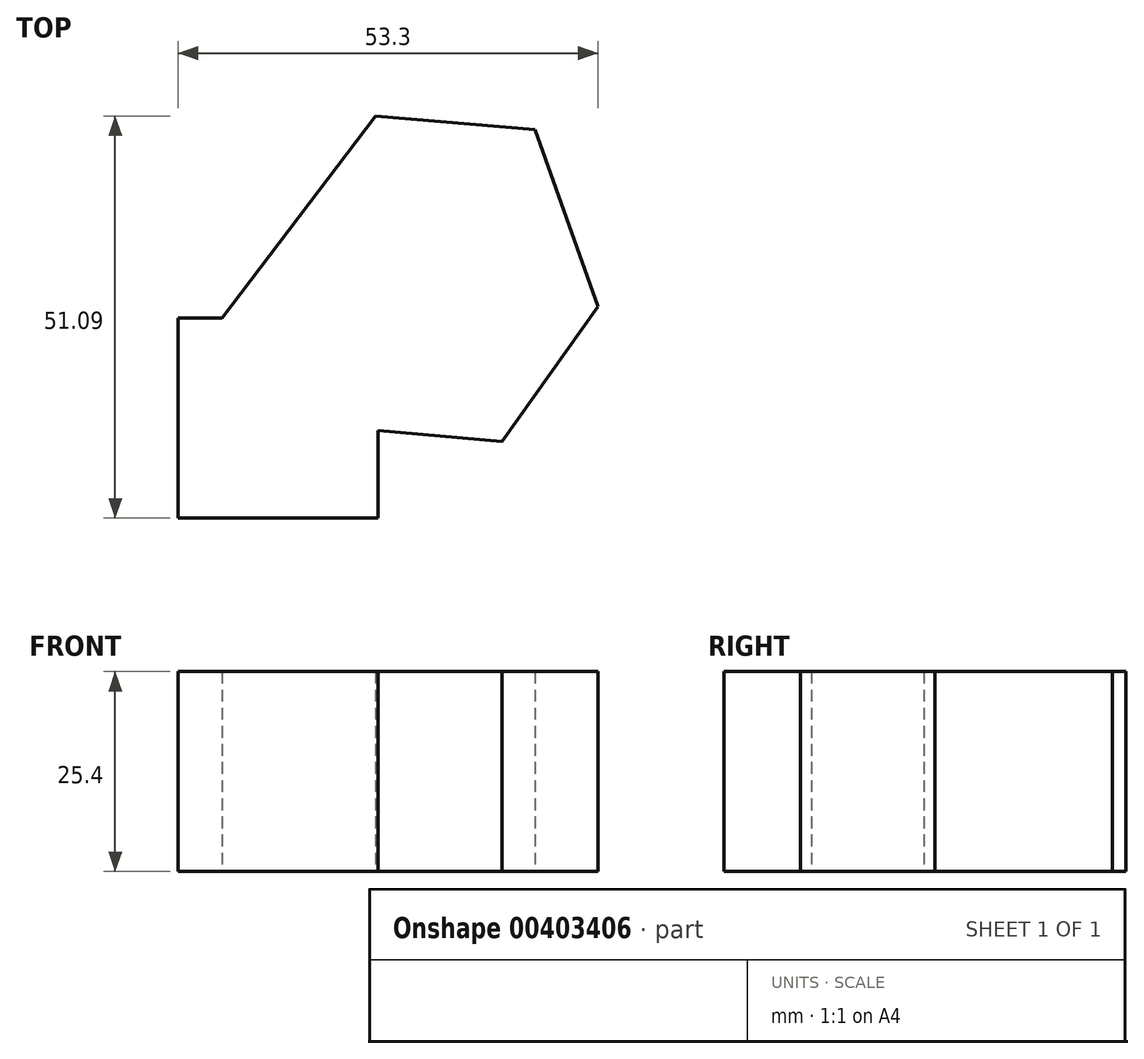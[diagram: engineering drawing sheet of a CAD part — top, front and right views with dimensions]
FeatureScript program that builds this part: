
annotation { "Feature Type Name" : "Feature", "Feature Type Description" : "" }
export const myFeature = defineFeature(function(context is Context, id is Id, definition is map)
    precondition{}
    {
        {
            var Q0;
            Q0=qCreatedBy(makeId("Top.planeOp"),FACE);
            var sketch = newSketch(context, id + "F0", { "sketchPlane" : qUnion([Q0])});
            skLineSegment(sketch, "E0.bottom", {"start": v(-30.25, -38.77) * mm, "end": v(-4.85, -38.77) * mm});
            skLineSegment(sketch, "E0.top", {"start": v(-30.25, -13.37) * mm, "end": v(-4.85, -13.37) * mm});
            skLineSegment(sketch, "E0.left", {"start": v(-30.25, -38.77) * mm, "end": v(-30.25, -13.37) * mm});
            skLineSegment(sketch, "E0.right", {"start": v(-4.85, -38.77) * mm, "end": v(-4.85, -13.37) * mm});
            skLineSegment(sketch, "E1", {"start": v(-26.63, -15.9) * mm, "end": v(-5.17, 12.32) * mm});
            skLineSegment(sketch, "E2", {"start": v(-5.17, 12.32) * mm, "end": v(15.1, 10.6) * mm});
            skLineSegment(sketch, "E3", {"start": v(15.1, 10.6) * mm, "end": v(23.05, -11.92) * mm});
            skLineSegment(sketch, "E4", {"start": v(23.05, -11.92) * mm, "end": v(10.86, -29.01) * mm});
            skLineSegment(sketch, "E5", {"start": v(10.86, -29.01) * mm, "end": v(-8.61, -27.29) * mm});
            skLineSegment(sketch, "E6", {"start": v(-8.61, -27.29) * mm, "end": v(-26.63, -15.9) * mm});
            skSolve(sketch);
        }
        {
            var Q0;
            {var subQ0=sQuery(id+"F0.wireOp",EDGE,"E6");Q0=makeQuery(id+"F0.imprint","IMPRINT",FACE,{"disambiguationData":[TD([[makeQuery(id+"F0.imprint","IMPRINT",EDGE,{"derivedFrom":subQ0}),-1.0]])]});}
            var Q1;
            {var subQ0=sQuery(id+"F0.wireOp",EDGE,"E2");Q1=makeQuery(id+"F0.imprint","IMPRINT",FACE,{"disambiguationData":[TD([[makeQuery(id+"F0.imprint","IMPRINT",EDGE,{"derivedFrom":subQ0}),-1.0]])]});}
            var Q2;
            {var subQ1=sQuery(id+"F0.wireOp",EDGE,"E0.bottom");Q2=makeQuery(id+"F0.imprint","IMPRINT",FACE,{"disambiguationData":[TD([[makeQuery(id+"F0.imprint","IMPRINT",EDGE,{"derivedFrom":subQ1}),1.0]])]});}
            extrude(context, id + "F1", {"entities" : qUnion([Q0, Q1, Q2]), "depth" : 25.4 * mm});
        }
    });
